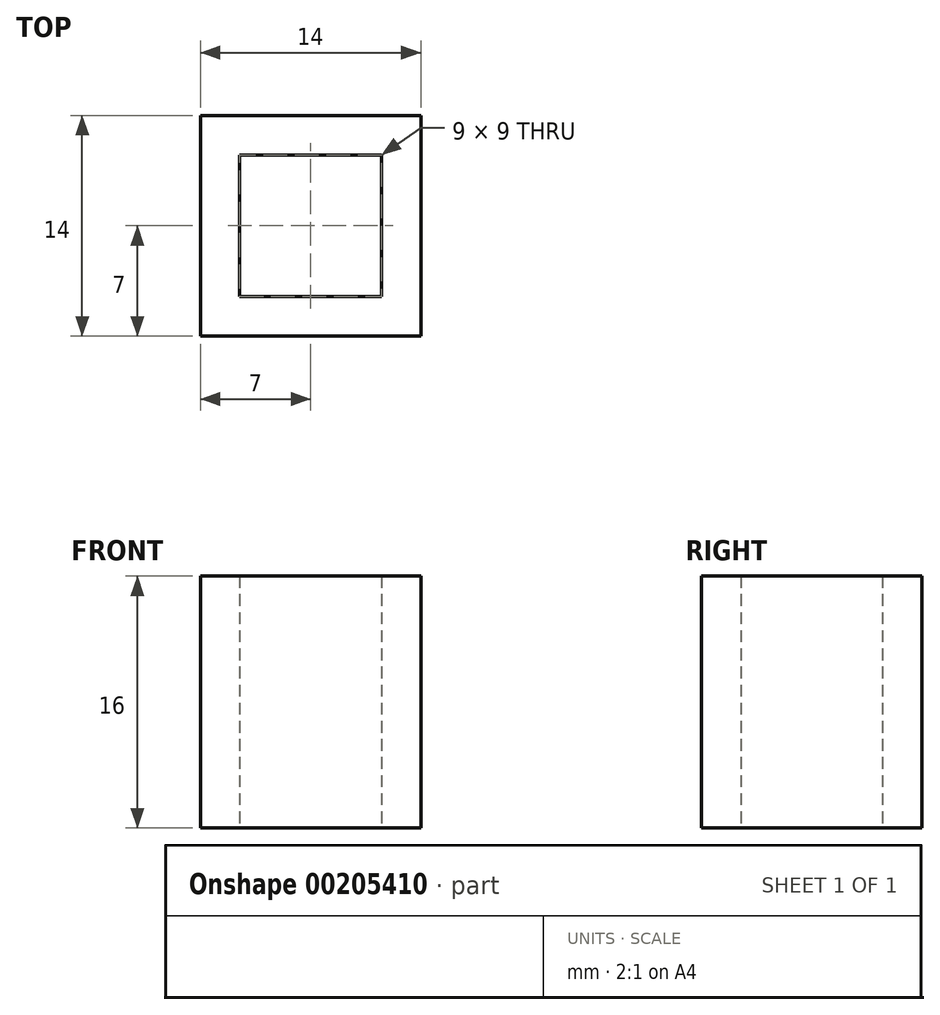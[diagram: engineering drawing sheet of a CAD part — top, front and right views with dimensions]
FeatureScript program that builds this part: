
annotation { "Feature Type Name" : "Feature", "Feature Type Description" : "" }
export const myFeature = defineFeature(function(context is Context, id is Id, definition is map)
    precondition{}
    {
        {
            var Q0;
            Q0=qCreatedBy(makeId("Top.planeOp"),FACE);
            var sketch = newSketch(context, id + "F0", { "sketchPlane" : qUnion([Q0])});
            skLineSegment(sketch, "E0.bottom", {"start": v(0, 0) * mm, "end": v(14, 0) * mm});
            skLineSegment(sketch, "E0.top", {"start": v(0, 14) * mm, "end": v(14, 14) * mm});
            skLineSegment(sketch, "E0.left", {"start": v(0, 0) * mm, "end": v(0, 14) * mm});
            skLineSegment(sketch, "E0.right", {"start": v(14, 0) * mm, "end": v(14, 14) * mm});
            skLineSegment(sketch, "E1.bottom", {"start": v(2.5, 2.5) * mm, "end": v(11.5, 2.5) * mm});
            skLineSegment(sketch, "E1.top", {"start": v(2.5, 11.5) * mm, "end": v(11.5, 11.5) * mm});
            skLineSegment(sketch, "E1.left", {"start": v(2.5, 2.5) * mm, "end": v(2.5, 11.5) * mm});
            skLineSegment(sketch, "E1.right", {"start": v(11.5, 2.5) * mm, "end": v(11.5, 11.5) * mm});
            skLineSegment(sketch, "E2", {"start": v(2.5, 7) * mm, "end": v(0, 7) * mm, "construction": true});
            skLineSegment(sketch, "E3", {"start": v(7, 11.5) * mm, "end": v(7, 14) * mm});
            skSolve(sketch);
        }
        {
            var Q0;
            Q0=makeQuery(id+"F0.imprint","IMPRINT",FACE,{"disambiguationData":[TD([[makeQuery(id+"F0.imprint","IMPRINT",EDGE,{"derivedFrom":sQuery(id+"F0.wireOp",EDGE,"E0.bottom")}),1.0]])]});
            extrude(context, id + "F1", {"entities" : qUnion([Q0]), "depth" : 16 * mm});
        }
    });
